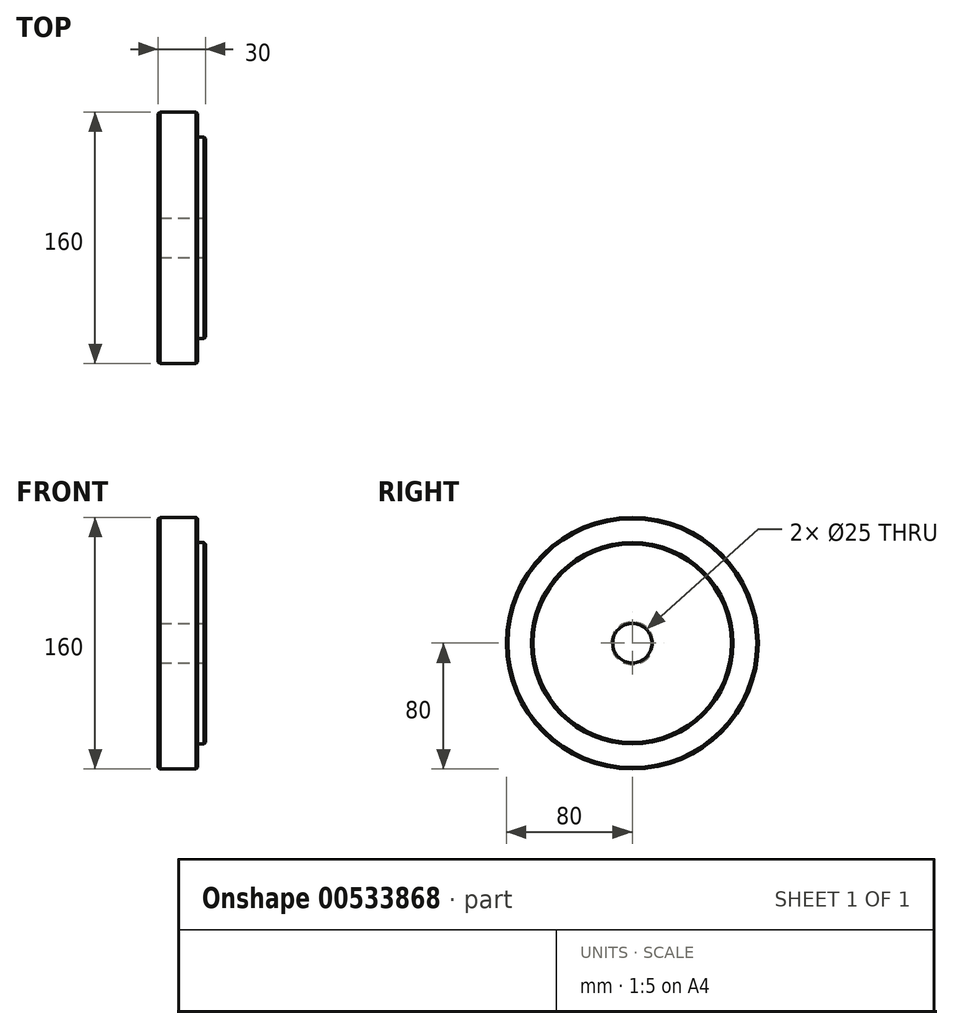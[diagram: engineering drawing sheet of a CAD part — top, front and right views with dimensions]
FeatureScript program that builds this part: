
annotation { "Feature Type Name" : "Feature", "Feature Type Description" : "" }
export const myFeature = defineFeature(function(context is Context, id is Id, definition is map)
    precondition{}
    {
        {
            var Q0;
            Q0=qCreatedBy(makeId("Front.planeOp"),FACE);
            var sketch = newSketch(context, id + "F0", { "sketchPlane" : qUnion([Q0])});
            skLineSegment(sketch, "E0", {"start": v(0, 80) * mm, "end": v(25, 80) * mm});
            skLineSegment(sketch, "E1", {"start": v(25, 80) * mm, "end": v(25, 64) * mm});
            skLineSegment(sketch, "E2", {"start": v(25, 64) * mm, "end": v(30, 64) * mm});
            skLineSegment(sketch, "E3", {"start": v(30, 64) * mm, "end": v(30, 0) * mm});
            skLineSegment(sketch, "E4", {"start": v(30, 0) * mm, "end": v(0, 0) * mm});
            skLineSegment(sketch, "E5", {"start": v(0, 0) * mm, "end": v(0, 80) * mm});
            skSolve(sketch);
        }
        {
            var Q0;
            Q0=makeQuery(id+"F0.imprint","IMPRINT",FACE,{"disambiguationData":[TD([[makeQuery(id+"F0.imprint","IMPRINT",EDGE,{"derivedFrom":sQuery(id+"F0.wireOp",EDGE,"E0")}),-1.0]])]});
            var Q1;
            Q1=sQuery(id+"F0.wireOp",EDGE,"E4");
            revolve(context, id + "F1", {"entities" : qUnion([Q0]), "axis" : qUnion([Q1]), "revolveType" : RevolveType.FULL});
        }
        {
            var Q0;
            Q0=makeQuery(id+"F1.opRevolve","SWEPT_FACE",FACE,{"disambiguationData":[OSD([sQuery(id+"F0.wireOp",EDGE,"E3")])]});
            var sketch = newSketch(context, id + "F2", { "sketchPlane" : qUnion([Q0])});
            skCircle(sketch, "E6", {"center": v(0, 0) * mm, "radius": 12.5 * mm});
            skSolve(sketch);
        }
        {
            var Q0;
            Q0=makeQuery(id+"F2.imprint","IMPRINT",FACE,{"disambiguationData":[TD([[makeQuery(id+"F2.imprint","IMPRINT",EDGE,{"derivedFrom":sQuery(id+"F2.wireOp",EDGE,"E6")}),1.0]])]});
            extrude(context, id + "F3", {"entities" : qUnion([Q0]), "operationType" : NewBodyOperationType.REMOVE, "oppositeDirection" : true, "depth" : 40 * mm, "offsetDistance" : 25 * mm});
        }
        {
            var Q0;
            Q0=makeQuery(id+"F1.opRevolve","SWEPT_EDGE",EDGE,{"disambiguationData":[OSD([sQuery(id+"F0.wireOp",EDGE,"E2"),sQuery(id+"F0.wireOp",EDGE,"E3")])]});
            var Q1;
            Q1=makeQuery(id+"F3.boolean.opBoolean","COPY",EDGE,{"derivedFrom":makeQuery(id+"F3.opExtrude","CAP_EDGE",EDGE,{"disambiguationData":[OSD([sQuery(id+"F2.wireOp",EDGE,"E6")])],"isStart":true})});
            var Q2;
            Q2=makeQuery(id+"F1.opRevolve","SWEPT_EDGE",EDGE,{"disambiguationData":[OSD([sQuery(id+"F0.wireOp",EDGE,"E0"),sQuery(id+"F0.wireOp",EDGE,"E1")])]});
            var Q3;
            Q3=makeQuery(id+"F1.opRevolve","SWEPT_EDGE",EDGE,{"disambiguationData":[OSD([sQuery(id+"F0.wireOp",EDGE,"E0"),sQuery(id+"F0.wireOp",EDGE,"E5")])]});
            var Q4;
            Q4=makeQuery(id+"F3.boolean.opBoolean","INTERSECT",EDGE,{"derivedFrom":[makeQuery(id+"F1.opRevolve","SWEPT_FACE",FACE,{"disambiguationData":[OSD([sQuery(id+"F0.wireOp",EDGE,"E5")])]}),makeQuery(id+"F3.opExtrude","SWEPT_FACE",FACE,{"disambiguationData":[OSD([sQuery(id+"F2.wireOp",EDGE,"E6")])]})]});
            chamfer(context, id + "F4", {"entities" : qUnion([Q0, Q1, Q2, Q3, Q4]), "width" : 1 * mm, "tangentPropagation" : true});
        }
    });
